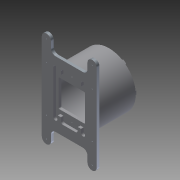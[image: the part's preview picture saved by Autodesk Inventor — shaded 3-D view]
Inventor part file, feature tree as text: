
AUTODESK INVENTOR PART (.ipt)
format: ipt  version: 2015 (Build 190159000, 159)  size: 447,488 bytes
history: native  units: in
note: dims shown in document units (in); Inventor stores cm internally (conversion verified against a paired STEP export)
features: direct_edit x5, move_body x5, other x4, extrude x3, sketch x3, imported_body x2, boolean_combine x1, reference x1
ambient origin geometry x8: Origin, YZ Plane, XZ Plane, XY Plane, X Axis, Y Axis, Z Axis, Center Point
bodies: Solid2 (feature_tree)
feature tree (24):
  other  "BetaSkeletonV011"
  direct_edit  "Direct Edit1"
  direct_edit  "Direct Edit2"
  extrude  "Extrusion1"  Depth=0.0394in
  direct_edit  "Direct Edit4"
  direct_edit  "Direct Edit5"
  direct_edit  "Direct Edit6"
  imported_body  "Base2"
  boolean_combine  "Combine1"
  extrude  "Extrusion2"  Depth=0.0059in TaperAngle=0.0deg
  extrude  "Extrusion3"  Depth=0.1969in
  imported_body  "Base1"
  sketch  "Sketch1"  dims[d0=0.0394in d1=0.0394in]
  sketch  "Sketch2"  dims[d2=0.0in d3=0.0in d4=-0.1378in d8=0.0in d9=0.0in d10=0.0059in]
  reference  "Reference1"
  sketch  "Sketch3"  dims[d11=0.0in d12=0.0in d13=0.0059in d14=2.2835in d15=1.3976in d16=0.0in d17=0.0in d18=0.0in d19=-0.125in d20=0.0in d21=0.0in d22=-0.125in d23=0.1969in d24=0.1969in d25=2.3622in d26=0.0in d27=0.9843in d28=0.9843in d29=2.3622in d30=0.0in]
  other  "Size1"
  other  "Size2"
  move_body  "Move1"
  move_body  "Move3"
  move_body  "Move4"
  other  "Size3"
  move_body  "Move5"
  move_body  "Move6"
